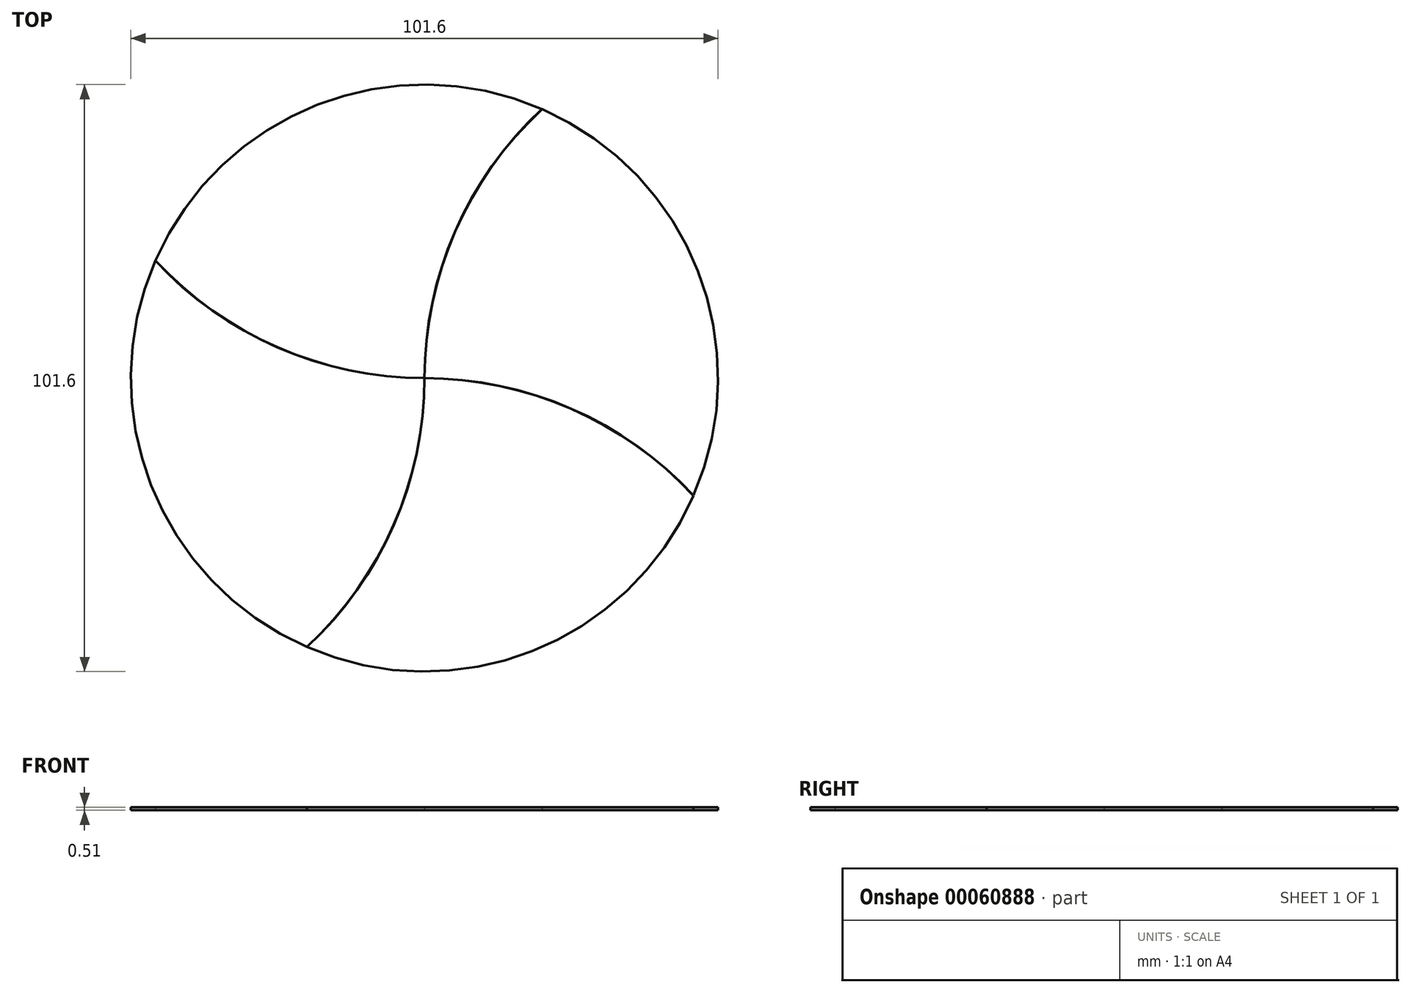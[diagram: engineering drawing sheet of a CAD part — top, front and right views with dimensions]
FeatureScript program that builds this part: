
annotation { "Feature Type Name" : "Feature", "Feature Type Description" : "" }
export const myFeature = defineFeature(function(context is Context, id is Id, definition is map)
    precondition{}
    {
        {
            var Q0;
            Q0=qCreatedBy(makeId("Top.planeOp"),FACE);
            var sketch = newSketch(context, id + "F0", { "sketchPlane" : qUnion([Q0])});
            skCircle(sketch, "E0", {"center": v(0, 0) * mm, "radius": 79.38 * mm, "construction": true});
            skCircle(sketch, "E1", {"center": v(0, 0) * mm, "radius": 63.5 * mm, "construction": true});
            skCircle(sketch, "E2", {"center": v(0, 0) * mm, "radius": 50.8 * mm, "construction": true});
            skCircle(sketch, "E3", {"center": v(0, 63.5) * mm, "radius": 63.5 * mm, "construction": true});
            skCircle(sketch, "E4", {"center": v(63.5, 0) * mm, "radius": 63.5 * mm, "construction": true});
            skCircle(sketch, "E5", {"center": v(-53.88, 44.45) * mm, "radius": 6.35 * mm, "construction": true});
            skCircle(sketch, "E6", {"center": v(19.05, 53.88) * mm, "radius": 6.35 * mm, "construction": true});
            skArc(sketch, "E7", {"start": v(-59.87, 42.33) * mm, "mid": v(-36.64, 11.68) * mm, "end": v(0, 0) * mm});
            skArc(sketch, "E8", {"start": v(-59.87, 42.33) * mm, "mid": v(-52.78, 50.7) * mm, "end": v(-48.98, 40.4) * mm});
            skArc(sketch, "E9", {"start": v(-48.98, 40.4) * mm, "mid": v(-16.97, 61.19) * mm, "end": v(21.17, 59.87) * mm});
            skArc(sketch, "E10", {"start": v(21.17, 59.87) * mm, "mid": v(25.3, 54.99) * mm, "end": v(23.1, 48.98) * mm});
            skArc(sketch, "E11", {"start": v(23.1, 48.98) * mm, "mid": v(6.06, 27.08) * mm, "end": v(0, 0) * mm});
            skCircle(sketch, "E12", {"center": v(-53.88, 44.45) * mm, "radius": 3.18 * mm});
            skCircle(sketch, "E13", {"center": v(19.05, 53.88) * mm, "radius": 3.18 * mm});
            skCircle(sketch, "E14", {"center": v(0, 0) * mm, "radius": 79.38 * mm});
            skCircle(sketch, "E15", {"center": v(0, 0) * mm, "radius": 63.5 * mm});
            skCircle(sketch, "E16", {"center": v(0, 0) * mm, "radius": 50.8 * mm});
            skSolve(sketch);
        }
        {
            var Q0;
            Q0=makeQuery(id+"F0.imprint","IMPRINT",FACE,{"disambiguationData":[TD([[makeQuery(id+"F0.imprint","IMPRINT",EDGE,{"derivedFrom":sQuery(id+"F0.wireOp",EDGE,"E7")}),1.0]])]});
            extrude(context, id + "F1", {"entities" : qUnion([Q0]), "depth" : 0.5 * mm});
        }
        {
            var Q0;
            Q0=makeQuery(id+"F1.opExtrude","SWEPT_BODY",BODY,{"disambiguationData":[OSD([sQuery(id+"F0.wireOp",EDGE,"E7"),sQuery(id+"F0.wireOp",EDGE,"E8"),sQuery(id+"F0.wireOp",EDGE,"E9"),sQuery(id+"F0.wireOp",EDGE,"E10"),sQuery(id+"F0.wireOp",EDGE,"E11"),sQuery(id+"F0.wireOp",EDGE,"E12"),sQuery(id+"F0.wireOp",EDGE,"E13")])]});
            var Q1;
            Q1=makeQuery(id+"F1.opExtrude","SWEPT_EDGE",EDGE,{"disambiguationData":[OSD([sQuery(id+"F0.wireOp",EDGE,"E7"),sQuery(id+"F0.wireOp",EDGE,"E11")])]});
            circularPattern(context, id + "F2", {"operationType" : NewBodyOperationType.ADD, "entities" : qUnion([Q0]), "axis" : qUnion([Q1]), "angle" : 360 * degree, "instanceCount" : 4, "equalSpace" : true});
        }
    });
